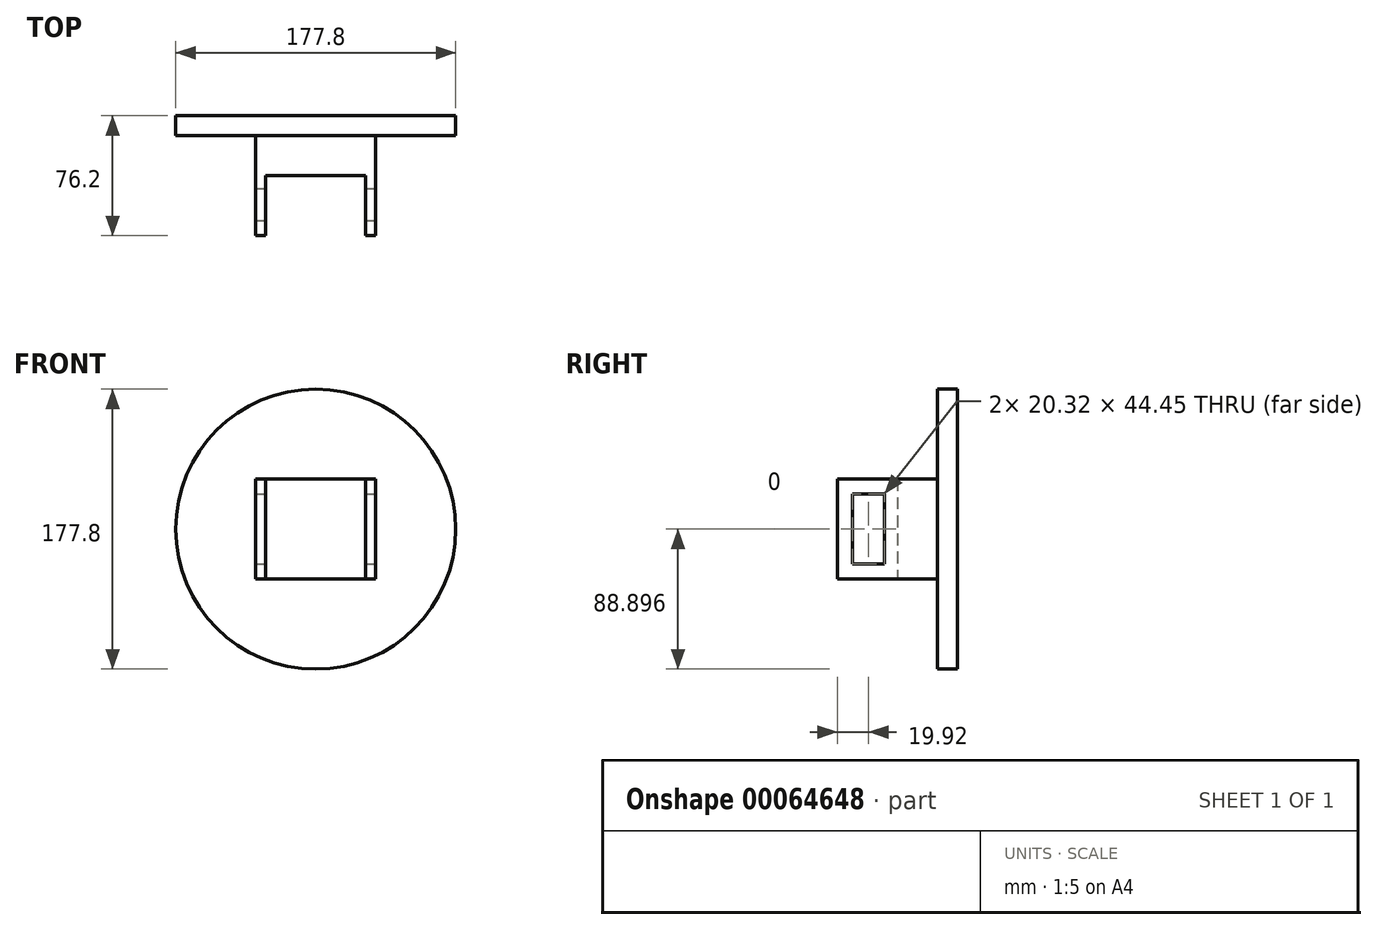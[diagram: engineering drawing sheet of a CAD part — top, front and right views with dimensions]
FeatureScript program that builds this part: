
annotation { "Feature Type Name" : "Feature", "Feature Type Description" : "" }
export const myFeature = defineFeature(function(context is Context, id is Id, definition is map)
    precondition{}
    {
        {
            var Q0;
            Q0=qCreatedBy(makeId("Front.planeOp"),FACE);
            var sketch = newSketch(context, id + "F0", { "sketchPlane" : qUnion([Q0])});
            skCircle(sketch, "E0", {"center": v(-827.72, 3.19) * mm, "radius": 88.9 * mm});
            skLineSegment(sketch, "E1.bottom", {"start": v(-865.82, 34.94) * mm, "end": v(-859.47, 34.94) * mm});
            skLineSegment(sketch, "E1.top", {"start": v(-865.82, -28.56) * mm, "end": v(-859.47, -28.56) * mm});
            skLineSegment(sketch, "E1.left", {"start": v(-865.82, 34.94) * mm, "end": v(-865.82, -28.56) * mm});
            skLineSegment(sketch, "E1.right", {"start": v(-859.47, 34.94) * mm, "end": v(-859.47, -28.56) * mm});
            skLineSegment(sketch, "E2", {"start": v(-827.72, 231.14) * mm, "end": v(-827.72, -214.68) * mm});
            skLineSegment(sketch, "E3", {"start": v(-1068.57, 3.19) * mm, "end": v(-468.04, 3.19) * mm});
            skLineSegment(sketch, "E4.MirrorCS", {"start": v(-795.97, 34.94) * mm, "end": v(-795.97, -28.56) * mm});
            skLineSegment(sketch, "E5.MirrorCS", {"start": v(-789.62, 34.94) * mm, "end": v(-789.62, -28.56) * mm});
            skLineSegment(sketch, "E6.MirrorCS", {"start": v(-789.62, 34.94) * mm, "end": v(-795.97, 34.94) * mm});
            skLineSegment(sketch, "E7.MirrorCS", {"start": v(-789.62, -28.56) * mm, "end": v(-795.97, -28.56) * mm});
            skLineSegment(sketch, "E8.bottom", {"start": v(-859.47, -28.56) * mm, "end": v(-795.97, -28.56) * mm});
            skLineSegment(sketch, "E8.top", {"start": v(-859.47, 34.94) * mm, "end": v(-795.97, 34.94) * mm});
            skLineSegment(sketch, "E8.left", {"start": v(-859.47, -28.56) * mm, "end": v(-859.47, 34.94) * mm});
            skLineSegment(sketch, "E8.right", {"start": v(-795.97, -28.56) * mm, "end": v(-795.97, 34.94) * mm});
            skSolve(sketch);
        }
        {
            var Q0;
            Q0=makeQuery(id+"F0.imprint","IMPRINT",FACE,{"disambiguationData":[TD([[makeQuery(id+"F0.imprint","IMPRINT",EDGE,{"derivedFrom":sQuery(id+"F0.wireOp",EDGE,"E0")}),1.0]])]});
            var Q1;
            {var subQ1=sQuery(id+"F0.wireOp",EDGE,"E1.top");Q1=makeQuery(id+"F0.imprint","IMPRINT",FACE,{"disambiguationData":[TD([[makeQuery(id+"F0.imprint","IMPRINT",EDGE,{"derivedFrom":subQ1}),-1.0]])]});}
            var Q2;
            {var subQ1=sQuery(id+"F0.wireOp",EDGE,"E1.bottom");Q2=makeQuery(id+"F0.imprint","IMPRINT",FACE,{"disambiguationData":[TD([[makeQuery(id+"F0.imprint","IMPRINT",EDGE,{"derivedFrom":subQ1}),1.0]])]});}
            extrude(context, id + "F1", {"entities" : qUnion([Q0, Q1, Q2]), "depth" : 12.7 * mm});
        }
        {
            var Q0;
            {var subQ0=sQuery(id+"F0.wireOp",EDGE,"E1.top");Q0=makeQuery(id+"F0.imprint","IMPRINT",FACE,{"disambiguationData":[TD([[makeQuery(id+"F0.imprint","IMPRINT",EDGE,{"derivedFrom":subQ0}),1.0]])]});}
            var Q1;
            {var subQ0=sQuery(id+"F0.wireOp",EDGE,"E1.bottom");Q1=makeQuery(id+"F0.imprint","IMPRINT",FACE,{"disambiguationData":[TD([[makeQuery(id+"F0.imprint","IMPRINT",EDGE,{"derivedFrom":subQ0}),-1.0]])]});}
            var Q2;
            {var subQ5=sQuery(id+"F0.wireOp",EDGE,"E7.MirrorCS");Q2=makeQuery(id+"F0.imprint","IMPRINT",FACE,{"disambiguationData":[TD([[makeQuery(id+"F0.imprint","IMPRINT",EDGE,{"derivedFrom":subQ5}),-1.0]])]});}
            var Q3;
            {var subQ5=sQuery(id+"F0.wireOp",EDGE,"E6.MirrorCS");Q3=makeQuery(id+"F0.imprint","IMPRINT",FACE,{"disambiguationData":[TD([[makeQuery(id+"F0.imprint","IMPRINT",EDGE,{"derivedFrom":subQ5}),1.0]])]});}
            extrude(context, id + "F2", {"entities" : qUnion([Q0, Q1, Q2, Q3]), "operationType" : NewBodyOperationType.ADD, "depth" : 76.2 * mm});
        }
        {
            var Q0;
            {var subQ0=sQuery(id+"F0.wireOp",EDGE,"E3");var subQ1=sQuery(id+"F0.wireOp",EDGE,"E2");var subQ2=makeQuery(id+"F0.imprint","INTERSECT",VERTEX,{"derivedFrom":[subQ1,subQ0]});Q0=makeQuery(id+"F0.imprint","IMPRINT",FACE,{"disambiguationData":[TD([[makeQuery(id+"F0.imprint","IMPRINT",EDGE,{"disambiguationData":[TD([[subQ2,-1.0]])],"derivedFrom":subQ1}),1.0]])]});}
            var Q1;
            {var subQ0=sQuery(id+"F0.wireOp",EDGE,"E3");var subQ1=sQuery(id+"F0.wireOp",EDGE,"E2");var subQ2=makeQuery(id+"F0.imprint","INTERSECT",VERTEX,{"derivedFrom":[subQ1,subQ0]});Q1=makeQuery(id+"F0.imprint","IMPRINT",FACE,{"disambiguationData":[TD([[makeQuery(id+"F0.imprint","IMPRINT",EDGE,{"disambiguationData":[TD([[subQ2,-1.0]])],"derivedFrom":subQ1}),-1.0]])]});}
            var Q2;
            {var subQ0=sQuery(id+"F0.wireOp",EDGE,"E8.top");var subQ1=sQuery(id+"F0.wireOp",EDGE,"E2");var subQ2=makeQuery(id+"F0.imprint","INTERSECT",VERTEX,{"derivedFrom":[subQ1,subQ0]});Q2=makeQuery(id+"F0.imprint","IMPRINT",FACE,{"disambiguationData":[TD([[makeQuery(id+"F0.imprint","IMPRINT",EDGE,{"disambiguationData":[TD([[subQ2,-1.0]])],"derivedFrom":subQ1}),-1.0]])]});}
            var Q3;
            {var subQ0=sQuery(id+"F0.wireOp",EDGE,"E8.top");var subQ1=sQuery(id+"F0.wireOp",EDGE,"E2");var subQ2=makeQuery(id+"F0.imprint","INTERSECT",VERTEX,{"derivedFrom":[subQ1,subQ0]});Q3=makeQuery(id+"F0.imprint","IMPRINT",FACE,{"disambiguationData":[TD([[makeQuery(id+"F0.imprint","IMPRINT",EDGE,{"disambiguationData":[TD([[subQ2,-1.0]])],"derivedFrom":subQ1}),1.0]])]});}
            extrude(context, id + "F3", {"entities" : qUnion([Q0, Q1, Q2, Q3]), "operationType" : NewBodyOperationType.ADD, "depth" : 38.1 * mm});
        }
        {
            var Q0;
            Q0=makeQuery(id+"F2.opExtrude","SWEPT_FACE",FACE,{"disambiguationData":[OSD([sQuery(id+"F0.wireOp",EDGE,"E5.MirrorCS")])]});
            var sketch = newSketch(context, id + "F4", { "sketchPlane" : qUnion([Q0])});
            skLineSegment(sketch, "E9.bottom", {"start": v(-66.44, -19.04) * mm, "end": v(-46.12, -19.04) * mm});
            skLineSegment(sketch, "E9.top", {"start": v(-66.44, 25.41) * mm, "end": v(-46.12, 25.41) * mm});
            skLineSegment(sketch, "E9.left", {"start": v(-66.44, -19.04) * mm, "end": v(-66.44, 25.41) * mm});
            skLineSegment(sketch, "E9.right", {"start": v(-46.12, -19.04) * mm, "end": v(-46.12, 25.41) * mm});
            skSolve(sketch);
        }
        {
            var Q0;
            Q0=makeQuery(id+"F4.imprint","IMPRINT",FACE,{"disambiguationData":[TD([[makeQuery(id+"F4.imprint","IMPRINT",EDGE,{"derivedFrom":sQuery(id+"F4.wireOp",EDGE,"E9.bottom")}),1.0]])]});
            extrude(context, id + "F5", {"entities" : qUnion([Q0]), "operationType" : NewBodyOperationType.REMOVE, "oppositeDirection" : true, "depth" : 200.03 * mm});
        }
    });
